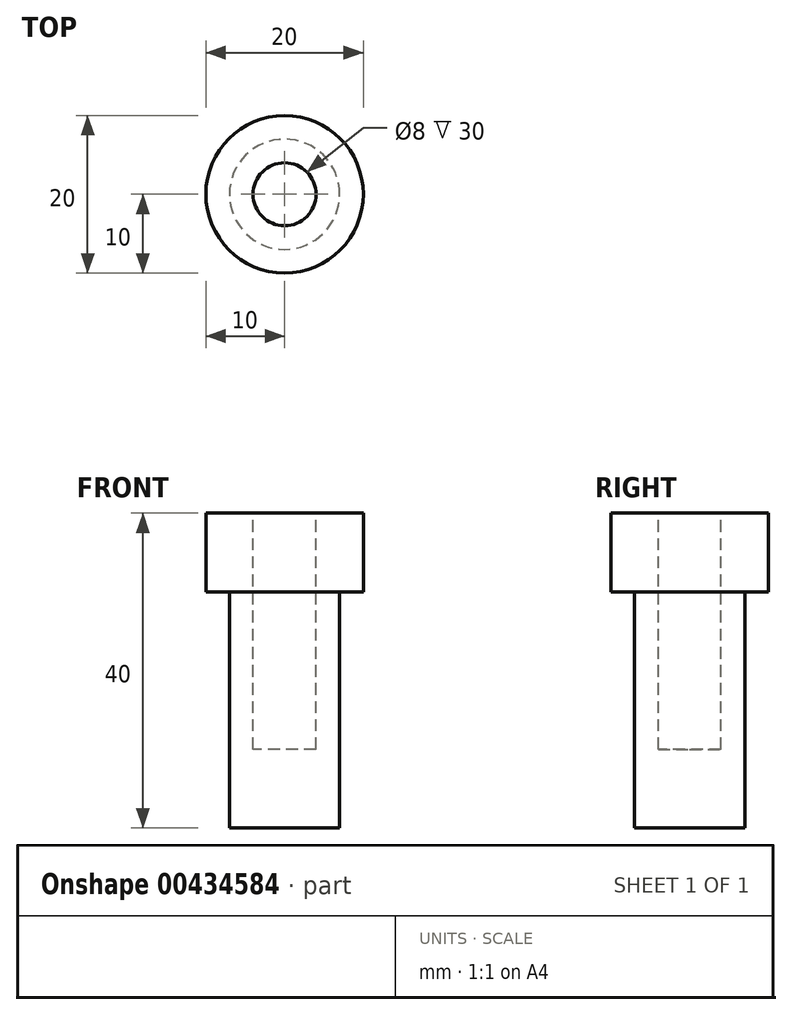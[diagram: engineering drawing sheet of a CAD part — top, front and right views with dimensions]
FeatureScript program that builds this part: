
annotation { "Feature Type Name" : "Feature", "Feature Type Description" : "" }
export const myFeature = defineFeature(function(context is Context, id is Id, definition is map)
    precondition{}
    {
        {
            var Q0;
            Q0=qCreatedBy(makeId("Top.planeOp"),FACE);
            var sketch = newSketch(context, id + "F0", { "sketchPlane" : qUnion([Q0])});
            skCircle(sketch, "E0", {"center": v(0, 0) * mm, "radius": 7 * mm});
            skCircle(sketch, "E1", {"center": v(0, 0) * mm, "radius": 10 * mm});
            skCircle(sketch, "E2", {"center": v(0, 0) * mm, "radius": 4 * mm});
            skSolve(sketch);
        }
        {
            var Q0;
            Q0=makeQuery(id+"F0.imprint","IMPRINT",FACE,{"disambiguationData":[TD([[makeQuery(id+"F0.imprint","IMPRINT",EDGE,{"derivedFrom":sQuery(id+"F0.wireOp",EDGE,"E0")}),1.0]])]});
            var Q1;
            Q1=makeQuery(id+"F0.imprint","IMPRINT",FACE,{"disambiguationData":[TD([[makeQuery(id+"F0.imprint","IMPRINT",EDGE,{"derivedFrom":sQuery(id+"F0.wireOp",EDGE,"E2")}),1.0]])]});
            extrude(context, id + "F1", {"entities" : qUnion([Q0, Q1]), "oppositeDirection" : true, "depth" : 30 * mm});
        }
        {
            var Q0;
            Q0=makeQuery(id+"F0.imprint","IMPRINT",FACE,{"disambiguationData":[TD([[makeQuery(id+"F0.imprint","IMPRINT",EDGE,{"derivedFrom":sQuery(id+"F0.wireOp",EDGE,"E2")}),1.0]])]});
            extrude(context, id + "F2", {"entities" : qUnion([Q0]), "operationType" : NewBodyOperationType.REMOVE, "oppositeDirection" : true, "depth" : 20 * mm});
        }
        {
            var Q0;
            Q0=makeQuery(id+"F0.imprint","IMPRINT",FACE,{"disambiguationData":[TD([[makeQuery(id+"F0.imprint","IMPRINT",EDGE,{"derivedFrom":sQuery(id+"F0.wireOp",EDGE,"E0")}),1.0]])]});
            var Q1;
            Q1=makeQuery(id+"F0.imprint","IMPRINT",FACE,{"disambiguationData":[TD([[makeQuery(id+"F0.imprint","IMPRINT",EDGE,{"derivedFrom":sQuery(id+"F0.wireOp",EDGE,"E0")}),-1.0]])]});
            extrude(context, id + "F3", {"entities" : qUnion([Q0, Q1]), "operationType" : NewBodyOperationType.ADD, "depth" : 10 * mm});
        }
    });
